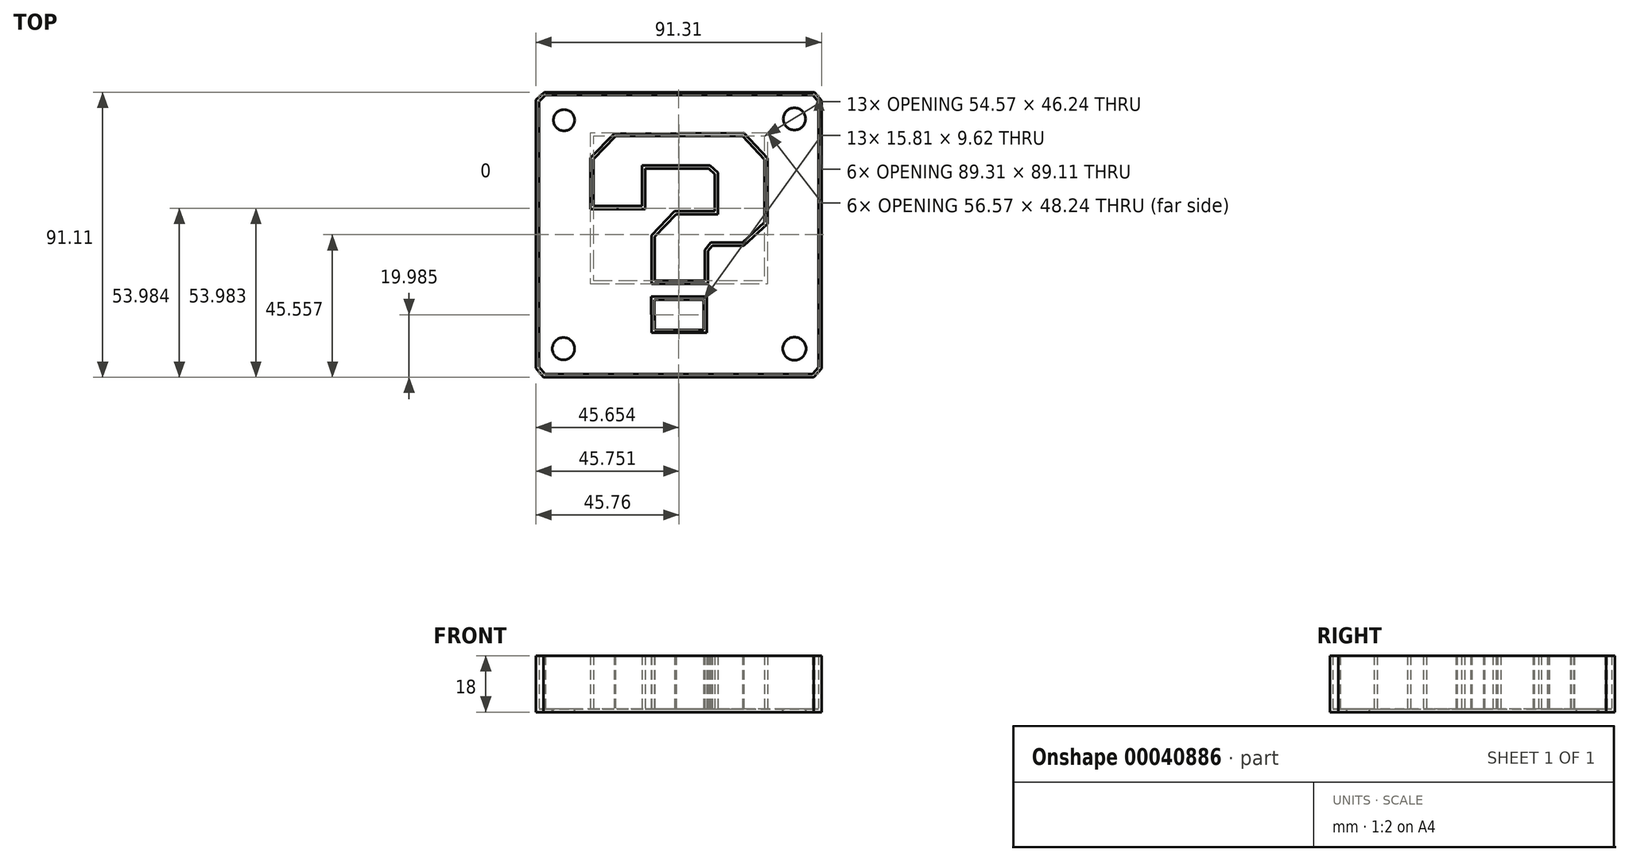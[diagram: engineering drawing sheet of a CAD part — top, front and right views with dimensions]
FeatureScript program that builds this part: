
annotation { "Feature Type Name" : "Feature", "Feature Type Description" : "" }
export const myFeature = defineFeature(function(context is Context, id is Id, definition is map)
    precondition{}
    {
        {
            var Q0;
            Q0=qCreatedBy(makeId("Top.planeOp"),FACE);
            var sketch = newSketch(context, id + "F0", { "sketchPlane" : qUnion([Q0])});
            skLineSegment(sketch, "E0", {"start": v(-45.72, 49.5) * mm, "end": v(-45.72, -35.36) * mm});
            skLineSegment(sketch, "E1", {"start": v(-45.72, -35.36) * mm, "end": v(-43.78, -37.68) * mm});
            skLineSegment(sketch, "E2", {"start": v(-43.78, -37.68) * mm, "end": v(41.65, -37.68) * mm});
            skLineSegment(sketch, "E3", {"start": v(41.65, -37.68) * mm, "end": v(43.59, -35.55) * mm});
            skLineSegment(sketch, "E4", {"start": v(43.59, -35.55) * mm, "end": v(43.59, 49.3) * mm});
            skLineSegment(sketch, "E5", {"start": v(43.59, 49.3) * mm, "end": v(41.85, 51.43) * mm});
            skLineSegment(sketch, "E6", {"start": v(41.85, 51.43) * mm, "end": v(-43.59, 51.43) * mm});
            skLineSegment(sketch, "E7", {"start": v(-43.59, 51.43) * mm, "end": v(-45.72, 49.5) * mm});
            skLineSegment(sketch, "E8", {"start": v(-21.7, 39.23) * mm, "end": v(-29.25, 31.48) * mm});
            skLineSegment(sketch, "E9", {"start": v(-29.25, 31.48) * mm, "end": v(-29.25, 15.01) * mm});
            skLineSegment(sketch, "E10", {"start": v(-29.25, 15.01) * mm, "end": v(-11.82, 15.01) * mm});
            skLineSegment(sketch, "E11", {"start": v(-11.82, 15.01) * mm, "end": v(-11.82, 26.44) * mm});
            skLineSegment(sketch, "E12", {"start": v(-11.82, 26.44) * mm, "end": v(-11.82, 28) * mm});
            skLineSegment(sketch, "E13", {"start": v(-11.82, 28) * mm, "end": v(8.52, 28) * mm});
            skLineSegment(sketch, "E14", {"start": v(8.52, 28) * mm, "end": v(10.46, 26.25) * mm});
            skLineSegment(sketch, "E15", {"start": v(10.46, 26.25) * mm, "end": v(10.46, 14.43) * mm});
            skLineSegment(sketch, "E16", {"start": v(10.46, 14.43) * mm, "end": v(-2.32, 14.43) * mm});
            skLineSegment(sketch, "E17", {"start": v(-2.32, 14.43) * mm, "end": v(-9.69, 6.68) * mm});
            skLineSegment(sketch, "E18", {"start": v(-9.69, 6.68) * mm, "end": v(-9.69, -8.81) * mm});
            skLineSegment(sketch, "E19", {"start": v(-9.69, -8.81) * mm, "end": v(8.33, -8.81) * mm});
            skLineSegment(sketch, "E20", {"start": v(8.33, -8.81) * mm, "end": v(8.33, 1.65) * mm});
            skLineSegment(sketch, "E21", {"start": v(8.33, 1.65) * mm, "end": v(9.69, 3.4) * mm});
            skLineSegment(sketch, "E22", {"start": v(9.69, 3.4) * mm, "end": v(19.76, 3.4) * mm});
            skLineSegment(sketch, "E23", {"start": v(19.76, 3.4) * mm, "end": v(27.32, 10.36) * mm});
            skLineSegment(sketch, "E24", {"start": v(27.32, 10.36) * mm, "end": v(27.32, 31.29) * mm});
            skLineSegment(sketch, "E25", {"start": v(27.32, 31.29) * mm, "end": v(19.76, 39.42) * mm});
            skLineSegment(sketch, "E26", {"start": v(19.76, 39.42) * mm, "end": v(-21.7, 39.23) * mm});
            skLineSegment(sketch, "E27", {"start": v(-9.88, -12.88) * mm, "end": v(7.94, -12.88) * mm});
            skLineSegment(sketch, "E28", {"start": v(7.94, -12.88) * mm, "end": v(7.94, -24.5) * mm});
            skLineSegment(sketch, "E29", {"start": v(7.94, -24.5) * mm, "end": v(-9.69, -24.5) * mm});
            skLineSegment(sketch, "E30", {"start": v(-9.69, -24.5) * mm, "end": v(-9.88, -12.88) * mm});
            skSolve(sketch);
        }
        {
            var Q0;
            Q0 = qSketchRegion(id + "F0", true);
            extrude(context, id + "F1", {"entities" : qUnion([Q0]), "depth" : 17 * mm});
        }
        {
            var Q0;
            Q0=makeQuery(id+"F1.opExtrude","CAP_FACE",FACE,{"disambiguationData":[OSD([sQuery(id+"F0.wireOp",EDGE,"E0"),sQuery(id+"F0.wireOp",EDGE,"E1"),sQuery(id+"F0.wireOp",EDGE,"E2"),sQuery(id+"F0.wireOp",EDGE,"E3"),sQuery(id+"F0.wireOp",EDGE,"E4"),sQuery(id+"F0.wireOp",EDGE,"E5"),sQuery(id+"F0.wireOp",EDGE,"E6"),sQuery(id+"F0.wireOp",EDGE,"E7"),sQuery(id+"F0.wireOp",EDGE,"E8"),sQuery(id+"F0.wireOp",EDGE,"E9"),sQuery(id+"F0.wireOp",EDGE,"E10"),sQuery(id+"F0.wireOp",EDGE,"E11"),sQuery(id+"F0.wireOp",EDGE,"E12"),sQuery(id+"F0.wireOp",EDGE,"E13"),sQuery(id+"F0.wireOp",EDGE,"E14"),sQuery(id+"F0.wireOp",EDGE,"E15"),sQuery(id+"F0.wireOp",EDGE,"E16"),sQuery(id+"F0.wireOp",EDGE,"E17"),sQuery(id+"F0.wireOp",EDGE,"E18"),sQuery(id+"F0.wireOp",EDGE,"E19"),sQuery(id+"F0.wireOp",EDGE,"E20"),sQuery(id+"F0.wireOp",EDGE,"E21"),sQuery(id+"F0.wireOp",EDGE,"E22"),sQuery(id+"F0.wireOp",EDGE,"E23"),sQuery(id+"F0.wireOp",EDGE,"E24"),sQuery(id+"F0.wireOp",EDGE,"E25"),sQuery(id+"F0.wireOp",EDGE,"E26"),sQuery(id+"F0.wireOp",EDGE,"E27"),sQuery(id+"F0.wireOp",EDGE,"E28"),sQuery(id+"F0.wireOp",EDGE,"E29"),sQuery(id+"F0.wireOp",EDGE,"E30")])],"isStart":false});
            shell(context, id + "F2", {"entities" : qUnion([Q0]), "thickness" : 1 * mm, "oppositeDirection" : true});
        }
        {
            var Q0;
            Q0=qCreatedBy(makeId("Top.planeOp"),FACE);
            var sketch = newSketch(context, id + "F3", { "sketchPlane" : qUnion([Q0])});
            skCircle(sketch, "E31", {"center": v(35.92, 43.86) * mm, "radius": 3.56 * mm});
            skCircle(sketch, "E32", {"center": v(-37.7, 43.47) * mm, "radius": 3.39 * mm});
            skCircle(sketch, "E33", {"center": v(35.92, -29.56) * mm, "radius": 3.7 * mm});
            skCircle(sketch, "E34", {"center": v(-37.89, -29.56) * mm, "radius": 3.56 * mm});
            skSolve(sketch);
        }
        {
            var Q0;
            Q0 = qSketchRegion(id + "F3", true);
            extrude(context, id + "F4", {"entities" : qUnion([Q0]), "operationType" : NewBodyOperationType.REMOVE, "oppositeDirection" : true, "depth" : 25 * mm});
        }
    });
